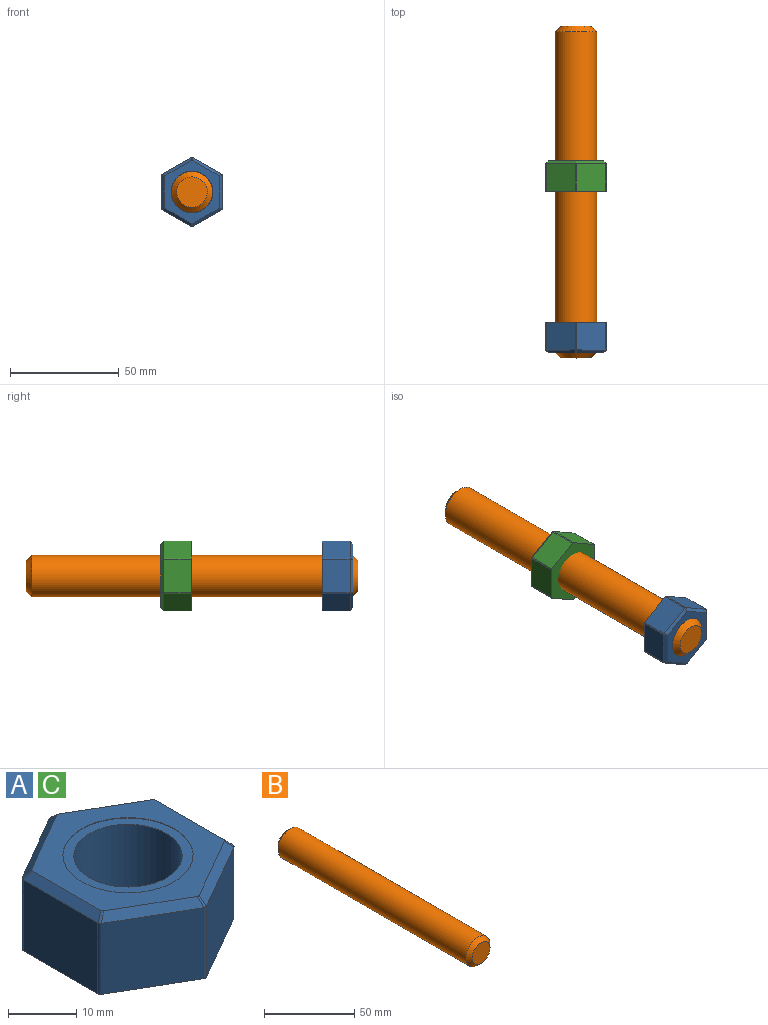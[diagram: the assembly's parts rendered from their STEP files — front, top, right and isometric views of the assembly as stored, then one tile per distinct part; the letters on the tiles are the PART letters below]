
ASSEMBLY  parts=3 mates=1
PART A: 29 faces, bbox 27.9x32.1x14 mm
  f0: plane 19.05x19.05mm, normal (0,0,1), area 87.1mm2, adj f2,f9
  f1: plane 32.05x27.93mm, normal (0,0,-1), area 477.5mm2, adj f2,f3,f4,f5,f6,f7,f8,f18
  f2: cylinder r=7.94mm len=15.88mm, axis (0,0,-1), area 692.8mm2, adj f0,f1
  f3: plane 15.39x12.7mm, normal (1,0,0), area 195.5mm2, adj f1,f14,f18,f26
  f4: plane 13.33x12.7mm, normal (0.5,-0.87,0), area 195.5mm2, adj f1,f12,f18,f20
  f5: plane 13.33x12.7mm, normal (-0.5,-0.87,0), area 195.5mm2, adj f1,f11,f20,f22
  f6: plane 15.39x12.7mm, normal (-1,0,0), area 195.5mm2, adj f1,f13,f22,f24
  f7: plane 13.33x12.7mm, normal (-0.5,0.87,0), area 195.5mm2, adj f1,f15,f24,f28
  f8: plane 13.33x12.7mm, normal (0.5,0.87,0), area 195.5mm2, adj f1,f16,f26,f28
  f9: cylinder r=9.53mm len=19.05mm, axis (0,0,-1), area 4.8mm2, adj f0,f10
  f10: plane 29.18x25.39mm, normal (0,0,1), area 273.2mm2, adj f9,f11,f12,f13,f14,f15,f16,f17
  f11: plane 13.51x8.53mm, normal (-0.35,-0.61,0.71), area 26.7mm2, adj f5,f10,f19,f20,f21,f22
  f12: plane 13.51x8.53mm, normal (0.35,-0.61,0.71), area 26.7mm2, adj f4,f10,f17,f18,f19,f20
  f13: plane 15.6x1.27mm, normal (-0.71,0,0.71), area 26.7mm2, adj f6,f10,f21,f22,f23,f24
  f14: plane 15.6x1.27mm, normal (0.71,0,0.71), area 26.7mm2, adj f3,f10,f17,f18,f25,f26
  f15: plane 13.51x8.53mm, normal (-0.35,0.61,0.71), area 26.7mm2, adj f7,f10,f23,f24,f27,f28
  f16: plane 13.51x8.53mm, normal (0.35,0.61,0.71), area 26.7mm2, adj f8,f10,f25,f26,f27,f28
  f17: cylinder r=0.64mm len=1.5mm, axis (0.65,-0.38,-0.65), area 0.9mm2, adj f10,f12,f14,f18
  f18: cylinder r=0.64mm len=12.73mm, axis (0,0,-1), area 8.5mm2, adj f1,f3,f4,f12,f14,f17
  f19: cylinder r=0.64mm len=1.5mm, axis (0,-0.76,-0.65), area 0.9mm2, adj f10,f11,f12,f20
  f20: cylinder r=0.64mm len=12.73mm, axis (0,0,-1), area 8.5mm2, adj f1,f4,f5,f11,f12,f19
  f21: cylinder r=0.64mm len=1.5mm, axis (0.65,0.38,0.65), area 0.9mm2, adj f10,f11,f13,f22
  f22: cylinder r=0.64mm len=12.73mm, axis (0,0,-1), area 8.5mm2, adj f1,f5,f6,f11,f13,f21
  f23: cylinder r=0.64mm len=1.5mm, axis (0.65,-0.38,0.65), area 0.9mm2, adj f10,f13,f15,f24
  f24: cylinder r=0.64mm len=12.73mm, axis (0,0,-1), area 8.5mm2, adj f1,f6,f7,f13,f15,f23
  f25: cylinder r=0.64mm len=1.5mm, axis (0.65,0.38,-0.65), area 0.9mm2, adj f10,f14,f16,f26
  f26: cylinder r=0.64mm len=12.73mm, axis (0,0,-1), area 8.5mm2, adj f1,f3,f8,f14,f16,f25
  f27: cylinder r=0.64mm len=1.5mm, axis (0,-0.76,0.65), area 0.9mm2, adj f10,f15,f16,f28
  f28: cylinder r=0.64mm len=12.73mm, axis (0,0,-1), area 8.5mm2, adj f1,f7,f8,f15,f16,f27
PART B: 5 faces, bbox 19.1x152.4x19.1 mm
  f0: cylinder r=9.53mm len=147.32mm, axis (0,1,0), area 8816.7mm2, adj f3,f4
  f1: plane 13.97x13.97mm, normal (0,-1,0), area 153.3mm2, adj f4
  f2: plane 13.97x13.97mm, normal (0,1,0), area 153.3mm2, adj f3
  f3: cone r=9.53mm half-angle=45deg, axis (0,-1,0), area 186.3mm2, adj f0,f2
  f4: cone r=6.99mm half-angle=45deg, axis (0,1,0), area 186.3mm2, adj f0,f1
PART C: same geometry as A
PLACE A rot(axis=(1,0,0),90deg) t=(-20.96,-78.41,-9.67)mm
PLACE B t=(-20.96,57.65,-9.67)mm
PLACE C rot(axis=(-1,0,0),90deg) t=(-20.96,-18.21,-9.67)mm
MATE fastened C.f2 <-> A.f2  axis (0,-1,0) through (-20.96,-18.21,-9.67)mm
